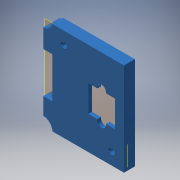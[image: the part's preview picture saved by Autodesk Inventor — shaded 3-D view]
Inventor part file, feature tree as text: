
AUTODESK INVENTOR PART (.ipt)
format: ipt  version: 2017 (Build 210142000, 142)  size: 280,064 bytes
history: native  units: in
note: dims shown in document units (in); Inventor stores cm internally (conversion verified against a paired STEP export)
features: reference x15, sketch x6, extrude x6, other x6, plane x4, fillet x2, chamfer x1
ambient origin geometry x8: Origin, YZ Plane, XZ Plane, XY Plane, X Axis, Y Axis, Z Axis, Center Point
bodies: Solid1 (feature_tree)
feature tree (40):
  plane  "Work Plane1"
  sketch  "Sketch1"  dims[d0=0.05in d1=1.0in d2=0.0in]
  plane  "Work Plane2"
  plane  "Work Plane4"
  extrude  "Extrusion1"  Depth=0.05in TaperAngle=0.0deg
  plane  "Work Plane3"
  extrude  "Extrusion3"  Depth=0.1in
  extrude  "Extrusion4"  Depth=0.2in TaperAngle=0.0deg
  chamfer  "Chamfer1"  Distance=0.025in Angle=45.0deg
  extrude  "Extrusion5"  Depth=0.1in
  extrude  "Extrusion6"  Depth=0.05in
  fillet  "Fillet1"  Radius=0.025in
  extrude  "Extrusion7"  Depth=0.05in TaperAngle=0.0deg
  fillet  "Fillet2"  Radius=0.05in
  reference  "Reference1"
  sketch  "Sketch2"  dims[d5=0.1in d6=0.0in d7=0.1in]
  reference  "Reference2"
  reference  "Reference3"
  reference  "Reference4"
  reference  "Reference5"
  reference  "Reference6"
  reference  "Reference7"
  sketch  "Sketch3"  dims[d8=0.1in d9=0.2in d10=0.0in]
  reference  "Reference8"
  reference  "Reference9"
  sketch  "Sketch5"  dims[d11=0.03in d12=0.025in d13=0.125in d14=45.0deg]
  reference  "Reference10"
  reference  "Reference11"
  reference  "Reference12"
  reference  "Reference13"
  sketch  "Sketch6"  dims[d15=1.0in d16=0.0in d17=0.1in]
  sketch  "Sketch7"  dims[d18=0.35in d19=0.0in d20=0.25in d21=0.025in d22=0.25in d23=0.0in d24=0.05in]
  reference  "Reference14"
  reference  "Reference15"
  other  "<userpath>\Documents\Inventor\PixyCam and Gimbal\Assembly2.iam"
  other  "Assembly2.iam"
  other  "PixyCamKinda:1"
  other  "backCase:1"
  other  "servo arm:1"
  other  "<userpath>\Documents\Inventor\PixyCam and Gimbal\Assembly2.iam"
